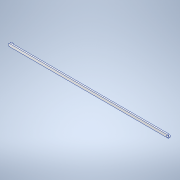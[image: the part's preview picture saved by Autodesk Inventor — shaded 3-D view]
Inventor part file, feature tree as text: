
AUTODESK INVENTOR PART (.ipt)
format: ipt  version: 2021 (Build 250183000, 183)  size: 111,616 bytes
history: native  units: in
note: dims shown in document units (in); Inventor stores cm internally (conversion verified against a paired STEP export)
features: extrude x3, sketch x3, other x1
ambient origin geometry x8: Origin, YZ Plane, XZ Plane, XY Plane, X Axis, Y Axis, Z Axis, Center Point
bodies: Body1 (feature_tree)
feature tree (7):
  other  "Sólido1"
  extrude  "Extrusión1"  Depth=14.3307in
  extrude  "Extrusión2"  Depth=0.125in TaperAngle=0.0deg
  extrude  "Extrusión3"  Depth=0.125in TaperAngle=0.0deg
  sketch  "Boceto1"  dims[d0=0.25in d1=14.3307in]
  sketch  "Boceto2"  dims[d2=0.25in d3=0.125in d4=0.0in]
  sketch  "Boceto3"  dims[d5=0.2106in d6=0.125in d7=0.0in d8=0.2106in d9=0.125in d10=0.0in]
